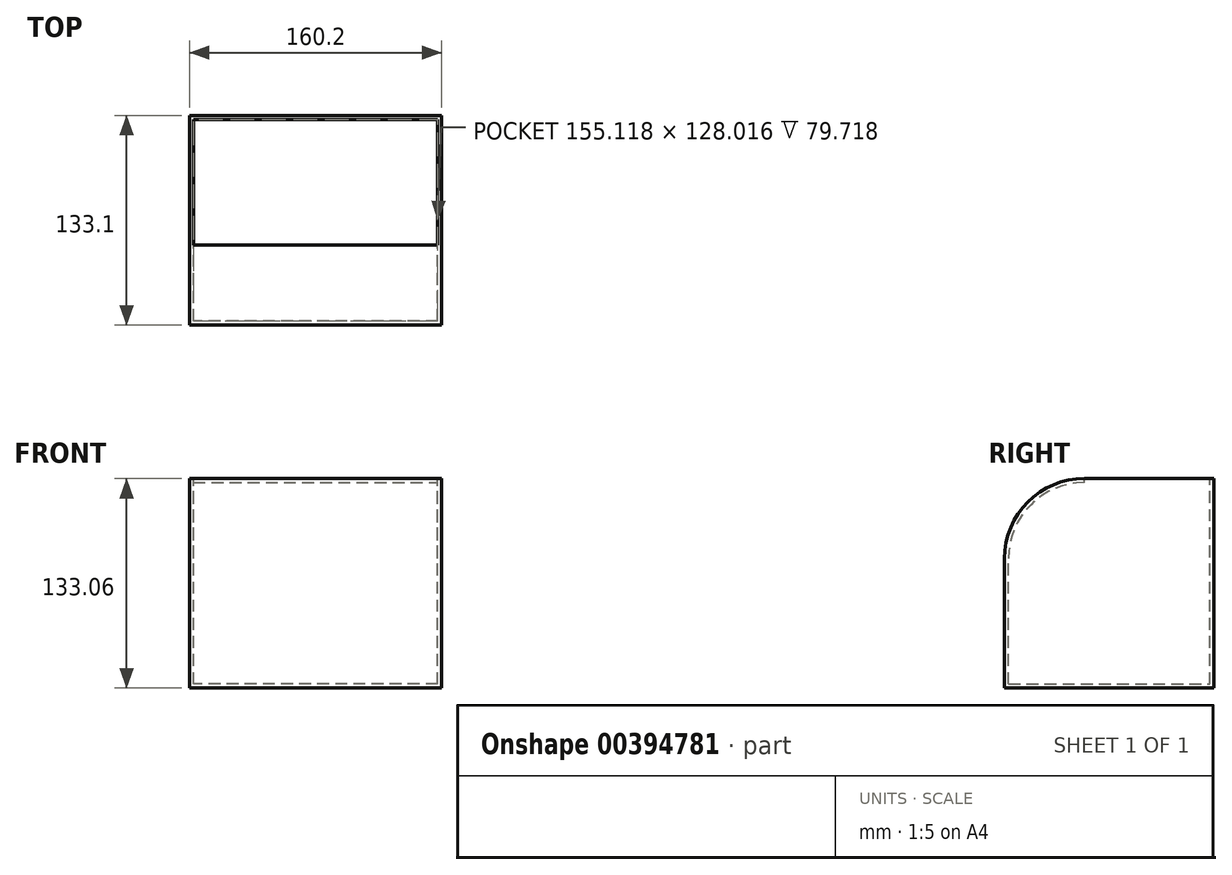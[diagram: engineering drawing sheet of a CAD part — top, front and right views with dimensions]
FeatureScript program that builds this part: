
annotation { "Feature Type Name" : "Feature", "Feature Type Description" : "" }
export const myFeature = defineFeature(function(context is Context, id is Id, definition is map)
    precondition{}
    {
        {
            var Q0;
            Q0=qCreatedBy(makeId("Front.planeOp"),FACE);
            var sketch = newSketch(context, id + "F0", { "sketchPlane" : qUnion([Q0])});
            skLineSegment(sketch, "E0.bottom", {"start": v(0, 0) * mm, "end": v(-160.2, 0) * mm});
            skLineSegment(sketch, "E0.top", {"start": v(0, 133.06) * mm, "end": v(-160.2, 133.06) * mm});
            skLineSegment(sketch, "E0.left", {"start": v(0, 0) * mm, "end": v(0, 133.06) * mm});
            skLineSegment(sketch, "E0.right", {"start": v(-160.2, 0) * mm, "end": v(-160.2, 133.06) * mm});
            skSolve(sketch);
        }
        {
            var Q0;
            Q0=makeQuery(id+"F0.imprint","IMPRINT",FACE,{"disambiguationData":[TD([[makeQuery(id+"F0.imprint","IMPRINT",EDGE,{"derivedFrom":sQuery(id+"F0.wireOp",EDGE,"E0.bottom")}),-1.0]])]});
            extrude(context, id + "F1", {"entities" : qUnion([Q0]), "depth" : 133.1 * mm, "hasSecondDirectionDraft" : true, "secondDirectionDraftAngle" : 3 * degree});
        }
        {
            var Q0;
            Q0=makeQuery(id+"F1.opExtrude","CAP_EDGE",EDGE,{"disambiguationData":[OSD([sQuery(id+"F0.wireOp",EDGE,"E0.top")])],"isStart":false});
            fillet(context, id + "F2", {"entities" : qUnion([Q0]), "radius" : 50.8 * mm, "tangentPropagation" : true, "allowEdgeOverflow" : false});
        }
        {
            var Q0;
            Q0=makeQuery(id+"F1.opExtrude","SWEPT_FACE",FACE,{"disambiguationData":[OSD([sQuery(id+"F0.wireOp",EDGE,"E0.top")])]});
            shell(context, id + "F3", {"entities" : qUnion([Q0]), "thickness" : 2.54 * mm});
        }
    });
